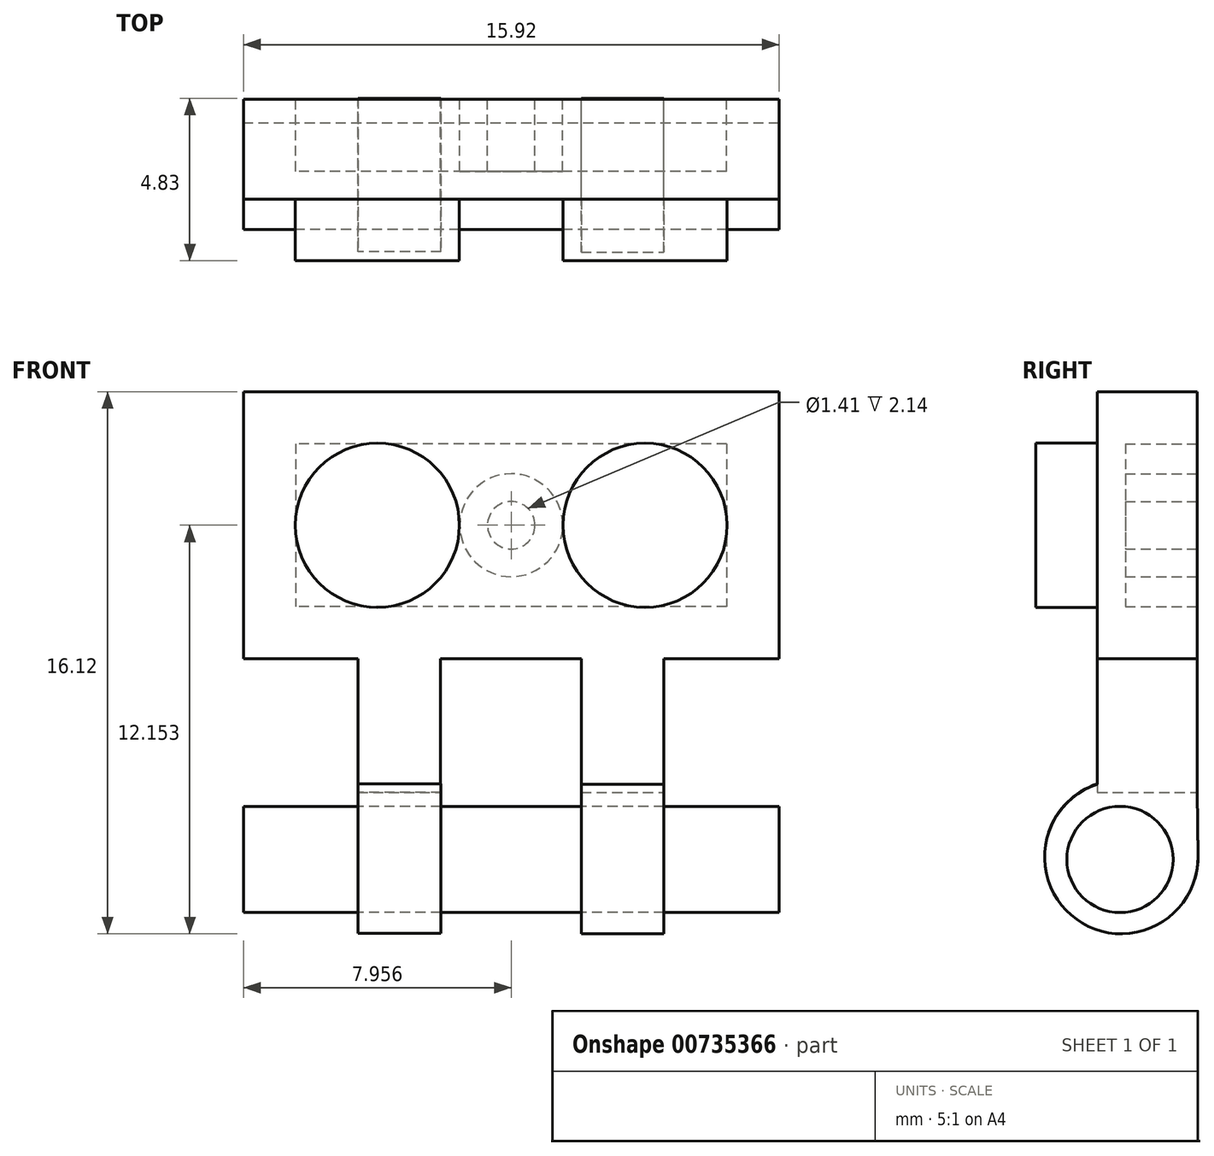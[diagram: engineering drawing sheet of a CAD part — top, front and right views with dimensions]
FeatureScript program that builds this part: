
annotation { "Feature Type Name" : "Feature", "Feature Type Description" : "" }
export const myFeature = defineFeature(function(context is Context, id is Id, definition is map)
    precondition{}
    {
        {
            var Q0;
            Q0=qCreatedBy(makeId("Front.planeOp"),FACE);
            var sketch = newSketch(context, id + "F0", { "sketchPlane" : qUnion([Q0])});
            skLineSegment(sketch, "E0.bottom", {"start": v(-5.25, 8.14) * mm, "end": v(10.67, 8.14) * mm});
            skLineSegment(sketch, "E0.top", {"start": v(-5.25, 0.2) * mm, "end": v(10.67, 0.2) * mm});
            skLineSegment(sketch, "E0.left", {"start": v(-5.25, 8.14) * mm, "end": v(-5.25, 0.2) * mm});
            skLineSegment(sketch, "E0.right", {"start": v(10.67, 8.14) * mm, "end": v(10.67, 0.2) * mm});
            skCircle(sketch, "E1", {"center": v(-1.27, 4.17) * mm, "radius": 2.44 * mm});
            skPoint(sketch, "E1.centerSnap0", {"position": v(-5.25, 4.17) * mm});
            skPoint(sketch, "E1.centerSnap1", {"position": v(-1.27, 8.14) * mm});
            skCircle(sketch, "E2", {"center": v(6.69, 4.17) * mm, "radius": 2.44 * mm});
            skPoint(sketch, "E2.centerSnap0", {"position": v(10.67, 4.17) * mm});
            skPoint(sketch, "E2.centerSnap1", {"position": v(6.69, 8.14) * mm});
            skPoint(sketch, "E3.end.orphan", {"position": v(2.7, 0.2) * mm});
            skPoint(sketch, "E3.start.orphan", {"position": v(2.7, 8.14) * mm});
            skPoint(sketch, "E4.start.orphan", {"position": v(-5.25, -1.33) * mm});
            skLineSegment(sketch, "E5", {"start": v(0.6, 0.2) * mm, "end": v(4.79, 0.2) * mm});
            skLineSegment(sketch, "E6", {"start": v(0.6, 0.2) * mm, "end": v(-1.85, 0.2) * mm});
            skLineSegment(sketch, "E7", {"start": v(4.79, 0.2) * mm, "end": v(7.25, 0.2) * mm});
            skLineSegment(sketch, "E8.bottom", {"start": v(-1.85, 0.2) * mm, "end": v(0.6, 0.2) * mm});
            skLineSegment(sketch, "E8.top", {"start": v(-1.85, -3.77) * mm, "end": v(0.6, -3.77) * mm});
            skLineSegment(sketch, "E8.left", {"start": v(-1.85, 0.2) * mm, "end": v(-1.85, -3.77) * mm});
            skLineSegment(sketch, "E8.right", {"start": v(0.6, 0.2) * mm, "end": v(0.6, -3.77) * mm});
            skLineSegment(sketch, "E9.top", {"start": v(4.79, -3.77) * mm, "end": v(7.25, -3.77) * mm});
            skLineSegment(sketch, "E9.left", {"start": v(4.79, 0.2) * mm, "end": v(4.79, -3.77) * mm});
            skLineSegment(sketch, "E9.right", {"start": v(7.25, 0.2) * mm, "end": v(7.25, -3.77) * mm});
            skSolve(sketch);
        }
        {
            var Q0;
            Q0 = qSketchRegion(id + "F0", true);
            extrude(context, id + "F1", {"entities" : qUnion([Q0]), "depth" : 2.97 * mm, "offsetDistance" : 25 * mm});
        }
        {
            var Q0;
            Q0=makeQuery(id+"F0.imprint","IMPRINT",FACE,{"disambiguationData":[TD([[makeQuery(id+"F0.imprint","IMPRINT",EDGE,{"derivedFrom":sQuery(id+"F0.wireOp",EDGE,"E1")}),1.0]])]});
            var Q1;
            Q1=makeQuery(id+"F0.imprint","IMPRINT",FACE,{"disambiguationData":[TD([[makeQuery(id+"F0.imprint","IMPRINT",EDGE,{"derivedFrom":sQuery(id+"F0.wireOp",EDGE,"E2")}),1.0]])]});
            extrude(context, id + "F2", {"entities" : qUnion([Q0, Q1]), "operationType" : NewBodyOperationType.ADD, "depth" : 4.8 * mm, "offsetDistance" : 25 * mm});
        }
        {
            var Q0;
            Q0=makeQuery(id+"F1.opExtrude","SWEPT_FACE",FACE,{"disambiguationData":[OSD([sQuery(id+"F0.wireOp",EDGE,"E8.left")])]});
            var sketch = newSketch(context, id + "F3", { "sketchPlane" : qUnion([Q0])});
            skArc(sketch, "E10", {"start": v(-0.03, -5.65) * mm, "mid": v(3.58, -7.54) * mm, "end": v(2.97, -3.52) * mm});
            skLineSegment(sketch, "E11", {"start": v(0, -3.77) * mm, "end": v(-0.03, -5.65) * mm});
            skLineSegment(sketch, "E12", {"start": v(0, -3.77) * mm, "end": v(2.97, -3.77) * mm});
            skLineSegment(sketch, "E13", {"start": v(2.97, -3.77) * mm, "end": v(2.97, -3.52) * mm});
            skPoint(sketch, "E14.end.orphan", {"position": v(0, -3.48) * mm});
            skSolve(sketch);
        }
        {
            var Q0;
            Q0 = qSketchRegion(id + "F3", true);
            extrude(context, id + "F4", {"entities" : qUnion([Q0]), "oppositeDirection" : true, "depth" : 2.47 * mm, "offsetDistance" : 25 * mm});
        }
        {
            var Q0;
            Q0=makeQuery(id+"F1.opExtrude","SWEPT_FACE",FACE,{"disambiguationData":[OSD([sQuery(id+"F0.wireOp",EDGE,"E9.right")])]});
            var sketch = newSketch(context, id + "F5", { "sketchPlane" : qUnion([Q0])});
            skArc(sketch, "E15", {"start": v(-2.97, -3.53) * mm, "mid": v(-3.59, -7.55) * mm, "end": v(0.02, -5.67) * mm});
            skLineSegment(sketch, "E16", {"start": v(0, -3.77) * mm, "end": v(0.02, -5.67) * mm});
            skLineSegment(sketch, "E17", {"start": v(0, -3.77) * mm, "end": v(-2.97, -3.77) * mm});
            skLineSegment(sketch, "E18", {"start": v(-2.97, -3.77) * mm, "end": v(-2.97, -3.53) * mm});
            skSolve(sketch);
        }
        {
            var Q0;
            Q0 = qSketchRegion(id + "F5", true);
            extrude(context, id + "F6", {"entities" : qUnion([Q0]), "operationType" : NewBodyOperationType.ADD, "oppositeDirection" : true, "depth" : 2.46 * mm, "offsetDistance" : 25 * mm});
        }
        {
            var Q0;
            Q0=makeQuery(id+"F1.opExtrude","SWEPT_FACE",FACE,{"disambiguationData":[OSD([sQuery(id+"F0.wireOp",EDGE,"E0.left")])]});
            var sketch = newSketch(context, id + "F7", { "sketchPlane" : qUnion([Q0])});
            skCircle(sketch, "E19", {"center": v(2.3, -5.77) * mm, "radius": 1.58 * mm});
            skSolve(sketch);
        }
        {
            var Q0;
            Q0 = qSketchRegion(id + "F7", true);
            extrude(context, id + "F8", {"entities" : qUnion([Q0]), "oppositeDirection" : true, "depth" : 15.92 * mm, "offsetDistance" : 25 * mm});
        }
        {
            var Q0;
            {var subQ0=sQuery(id+"F0.wireOp",EDGE,"E2");var subQ1=sQuery(id+"F0.wireOp",EDGE,"E1");Q0=makeQuery(id+"F2.boolean.opBoolean","MERGE",FACE,{"derivedFrom":[makeQuery(id+"F1.opExtrude","CAP_FACE",FACE,{"disambiguationData":[OSD([sQuery(id+"F0.wireOp",EDGE,"E0.bottom"),sQuery(id+"F0.wireOp",EDGE,"E0.top"),sQuery(id+"F0.wireOp",EDGE,"E0.left"),sQuery(id+"F0.wireOp",EDGE,"E0.right"),subQ1,subQ0,sQuery(id+"F0.wireOp",EDGE,"E5"),sQuery(id+"F0.wireOp",EDGE,"E8.top"),sQuery(id+"F0.wireOp",EDGE,"E8.left"),sQuery(id+"F0.wireOp",EDGE,"E8.right"),sQuery(id+"F0.wireOp",EDGE,"E9.top"),sQuery(id+"F0.wireOp",EDGE,"E9.left"),sQuery(id+"F0.wireOp",EDGE,"E9.right")])],"isStart":true}),makeQuery(id+"F2.opExtrude","CAP_FACE",FACE,{"disambiguationData":[OSD([subQ1])],"isStart":true}),makeQuery(id+"F2.opExtrude","CAP_FACE",FACE,{"disambiguationData":[OSD([subQ0])],"isStart":true})]});}
            var sketch = newSketch(context, id + "F9", { "sketchPlane" : qUnion([Q0])});
            skLineSegment(sketch, "E20.bottom", {"start": v(-9.12, 6.6) * mm, "end": v(3.7, 6.6) * mm});
            skLineSegment(sketch, "E20.top", {"start": v(-9.12, 1.75) * mm, "end": v(3.7, 1.75) * mm});
            skLineSegment(sketch, "E20.left", {"start": v(-9.12, 6.6) * mm, "end": v(-9.12, 1.75) * mm});
            skLineSegment(sketch, "E20.right", {"start": v(3.7, 6.6) * mm, "end": v(3.7, 1.75) * mm});
            skCircle(sketch, "E21", {"center": v(-2.7, 4.17) * mm, "radius": 1.53 * mm});
            skCircle(sketch, "E22", {"center": v(-2.7, 4.17) * mm, "radius": 0.7 * mm});
            skPoint(sketch, "E23.start.orphan", {"position": v(-10.67, 4.17) * mm});
            skPoint(sketch, "E24.start.orphan", {"position": v(-2.7, 8.14) * mm});
            skPoint(sketch, "E25.trimOffspring.end.orphan", {"position": v(-2.7, 0.2) * mm});
            skPoint(sketch, "E26.trimOffspring.end.orphan", {"position": v(5.25, 4.17) * mm});
            skLineSegment(sketch, "E27.bottom", {"start": v(-10.67, 8.14) * mm, "end": v(5.25, 8.14) * mm});
            skLineSegment(sketch, "E27.top", {"start": v(-10.67, 0.2) * mm, "end": v(5.25, 0.2) * mm});
            skLineSegment(sketch, "E27.left", {"start": v(-10.67, 8.14) * mm, "end": v(-10.67, 0.2) * mm});
            skLineSegment(sketch, "E27.right", {"start": v(5.25, 8.14) * mm, "end": v(5.25, 0.2) * mm});
            skSolve(sketch);
        }
        {
            var Q0;
            Q0=makeQuery(id+"F9.imprint","IMPRINT",FACE,{"disambiguationData":[TD([[makeQuery(id+"F9.imprint","IMPRINT",EDGE,{"derivedFrom":sQuery(id+"F9.wireOp",EDGE,"E20.left")}),1.0]])]});
            var Q1;
            Q1=makeQuery(id+"F9.imprint","IMPRINT",FACE,{"disambiguationData":[TD([[makeQuery(id+"F9.imprint","IMPRINT",EDGE,{"derivedFrom":sQuery(id+"F9.wireOp",EDGE,"E22")}),1.0]])]});
            extrude(context, id + "F10", {"entities" : qUnion([Q0, Q1]), "operationType" : NewBodyOperationType.REMOVE, "oppositeDirection" : true, "depth" : 2.14 * mm, "offsetDistance" : 25 * mm});
        }
    });
